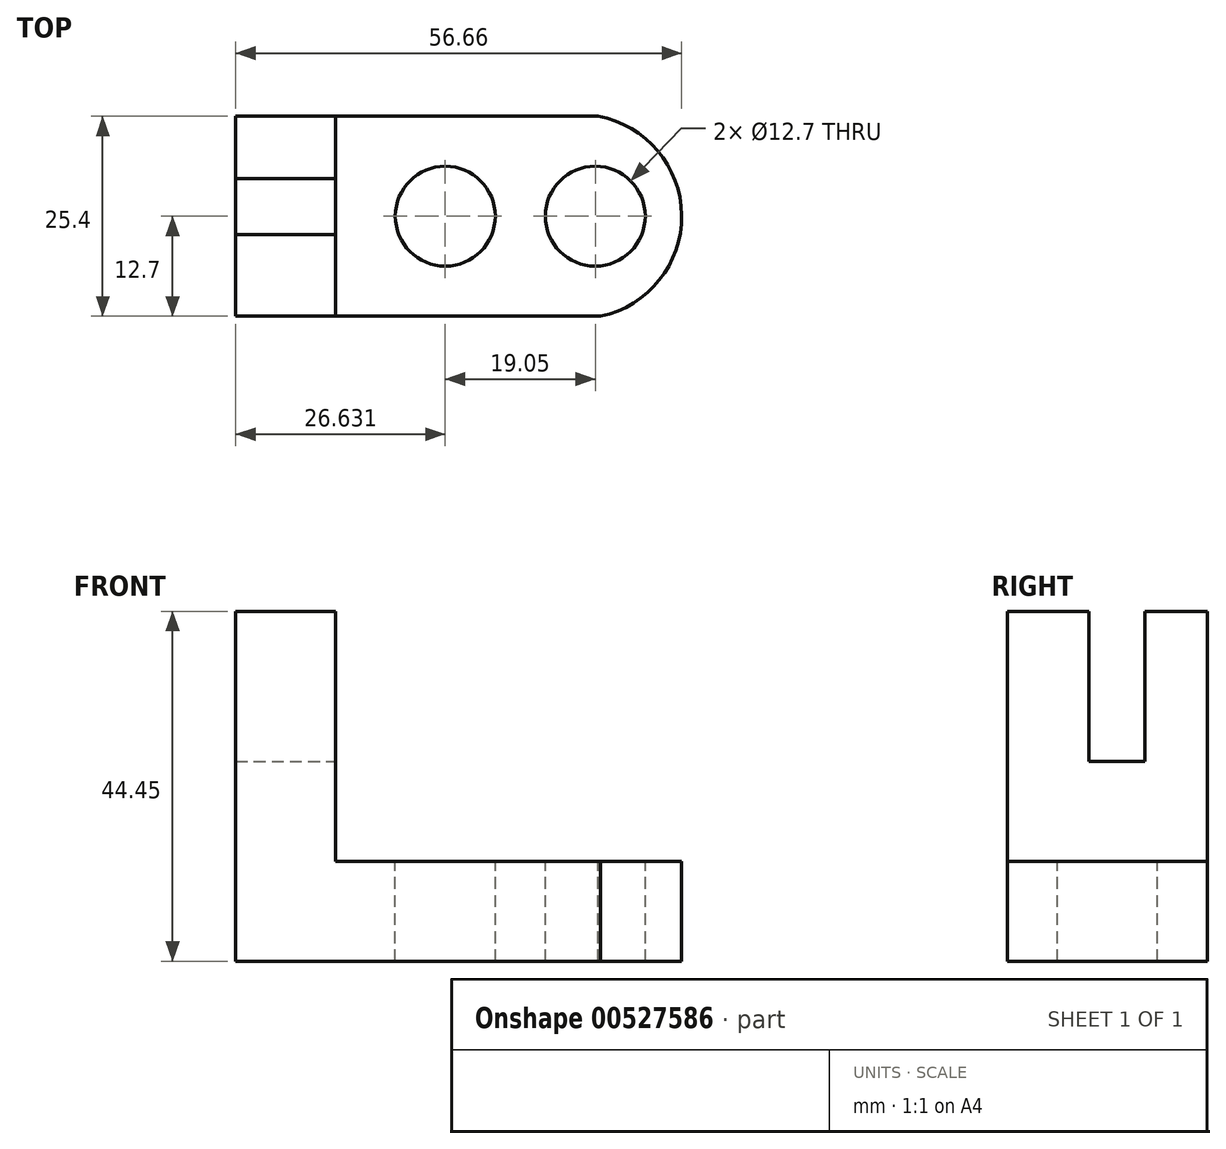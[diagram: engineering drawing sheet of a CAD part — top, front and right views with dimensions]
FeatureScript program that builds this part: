
annotation { "Feature Type Name" : "Feature", "Feature Type Description" : "" }
export const myFeature = defineFeature(function(context is Context, id is Id, definition is map)
    precondition{}
    {
        {
            var Q0;
            Q0=qCreatedBy(makeId("Front.planeOp"),FACE);
            var sketch = newSketch(context, id + "F0", { "sketchPlane" : qUnion([Q0])});
            skLineSegment(sketch, "E0", {"start": v(0, 0) * mm, "end": v(57.15, 0) * mm});
            skLineSegment(sketch, "E1", {"start": v(57.15, 0) * mm, "end": v(57.15, 12.7) * mm});
            skLineSegment(sketch, "E2", {"start": v(57.15, 12.7) * mm, "end": v(12.7, 12.7) * mm});
            skLineSegment(sketch, "E3", {"start": v(12.7, 12.7) * mm, "end": v(12.7, 44.45) * mm});
            skLineSegment(sketch, "E4", {"start": v(12.7, 44.45) * mm, "end": v(0, 44.45) * mm});
            skLineSegment(sketch, "E5", {"start": v(0, 44.45) * mm, "end": v(0, 0) * mm});
            skSolve(sketch);
        }
        {
            var Q0;
            Q0=makeQuery(id+"F0.imprint","IMPRINT",FACE,{"disambiguationData":[TD([[makeQuery(id+"F0.imprint","IMPRINT",EDGE,{"derivedFrom":sQuery(id+"F0.wireOp",EDGE,"E0")}),1.0]])]});
            extrude(context, id + "F1", {"entities" : qUnion([Q0]), "depth" : 25.4 * mm, "offsetDistance" : 25.4 * mm});
        }
        {
            var Q0;
            Q0=makeQuery(id+"F1.opExtrude","SWEPT_FACE",FACE,{"disambiguationData":[OSD([sQuery(id+"F0.wireOp",EDGE,"E3")])]});
            var sketch = newSketch(context, id + "F2", { "sketchPlane" : qUnion([Q0])});
            skSolve(sketch);
        }
        {
            var Q0;
            Q0=makeQuery(id+"F1.opExtrude","SWEPT_FACE",FACE,{"disambiguationData":[OSD([sQuery(id+"F0.wireOp",EDGE,"E2")])]});
            var sketch = newSketch(context, id + "F3", { "sketchPlane" : qUnion([Q0])});
            skCircle(sketch, "E6", {"center": v(26.63, -12.7) * mm, "radius": 6.35 * mm});
            skCircle(sketch, "E7", {"center": v(45.68, -12.7) * mm, "radius": 6.35 * mm});
            skSolve(sketch);
        }
        {
            var Q0;
            Q0=makeQuery(id+"F3.imprint","IMPRINT",FACE,{"disambiguationData":[TD([[makeQuery(id+"F3.imprint","IMPRINT",EDGE,{"derivedFrom":sQuery(id+"F3.wireOp",EDGE,"E6")}),1.0]])]});
            var Q1;
            Q1=makeQuery(id+"F3.imprint","IMPRINT",FACE,{"disambiguationData":[TD([[makeQuery(id+"F3.imprint","IMPRINT",EDGE,{"derivedFrom":sQuery(id+"F3.wireOp",EDGE,"E7")}),1.0]])]});
            extrude(context, id + "F4", {"entities" : qUnion([Q0, Q1]), "operationType" : NewBodyOperationType.REMOVE, "oppositeDirection" : true, "depth" : 25.4 * mm, "offsetDistance" : 25.4 * mm});
        }
        {
            var Q0;
            Q0=makeQuery(id+"F1.opExtrude","SWEPT_FACE",FACE,{"disambiguationData":[OSD([sQuery(id+"F0.wireOp",EDGE,"E2")])]});
            var sketch = newSketch(context, id + "F5", { "sketchPlane" : qUnion([Q0])});
            skArc(sketch, "E8", {"start": v(46.36, -25.4) * mm, "mid": v(56.65, -12.57) * mm, "end": v(46.05, 0) * mm});
            skSolve(sketch);
        }
        {
            var Q0;
            {var subQ0=sQuery(id+"F5.wireOp",EDGE,"E8");Q0=makeQuery(id+"F5.imprint","IMPRINT",FACE,{"disambiguationData":[TD([[makeQuery(id+"F5.imprint","IMPRINT",EDGE,{"derivedFrom":subQ0}),-1.0]])]});}
            extrude(context, id + "F6", {"entities" : qUnion([Q0]), "operationType" : NewBodyOperationType.REMOVE, "oppositeDirection" : true, "depth" : 25.4 * mm, "offsetDistance" : 25.4 * mm});
        }
        {
            var Q0;
            Q0=makeQuery(id+"F1.opExtrude","SWEPT_FACE",FACE,{"disambiguationData":[OSD([sQuery(id+"F0.wireOp",EDGE,"E4")])]});
            var sketch = newSketch(context, id + "F7", { "sketchPlane" : qUnion([Q0])});
            skLineSegment(sketch, "E9", {"start": v(0, -7.9) * mm, "end": v(12.7, -7.9) * mm});
            skLineSegment(sketch, "E10", {"start": v(0, -15.04) * mm, "end": v(12.7, -15.04) * mm});
            skSolve(sketch);
        }
        {
            var Q0;
            {var subQ0=sQuery(id+"F7.wireOp",EDGE,"E9");Q0=makeQuery(id+"F7.imprint","IMPRINT",FACE,{"disambiguationData":[TD([[makeQuery(id+"F7.imprint","IMPRINT",EDGE,{"derivedFrom":subQ0}),-1.0]])]});}
            extrude(context, id + "F8", {"entities" : qUnion([Q0]), "operationType" : NewBodyOperationType.REMOVE, "oppositeDirection" : true, "depth" : 19.05 * mm, "offsetDistance" : 25.4 * mm});
        }
    });
